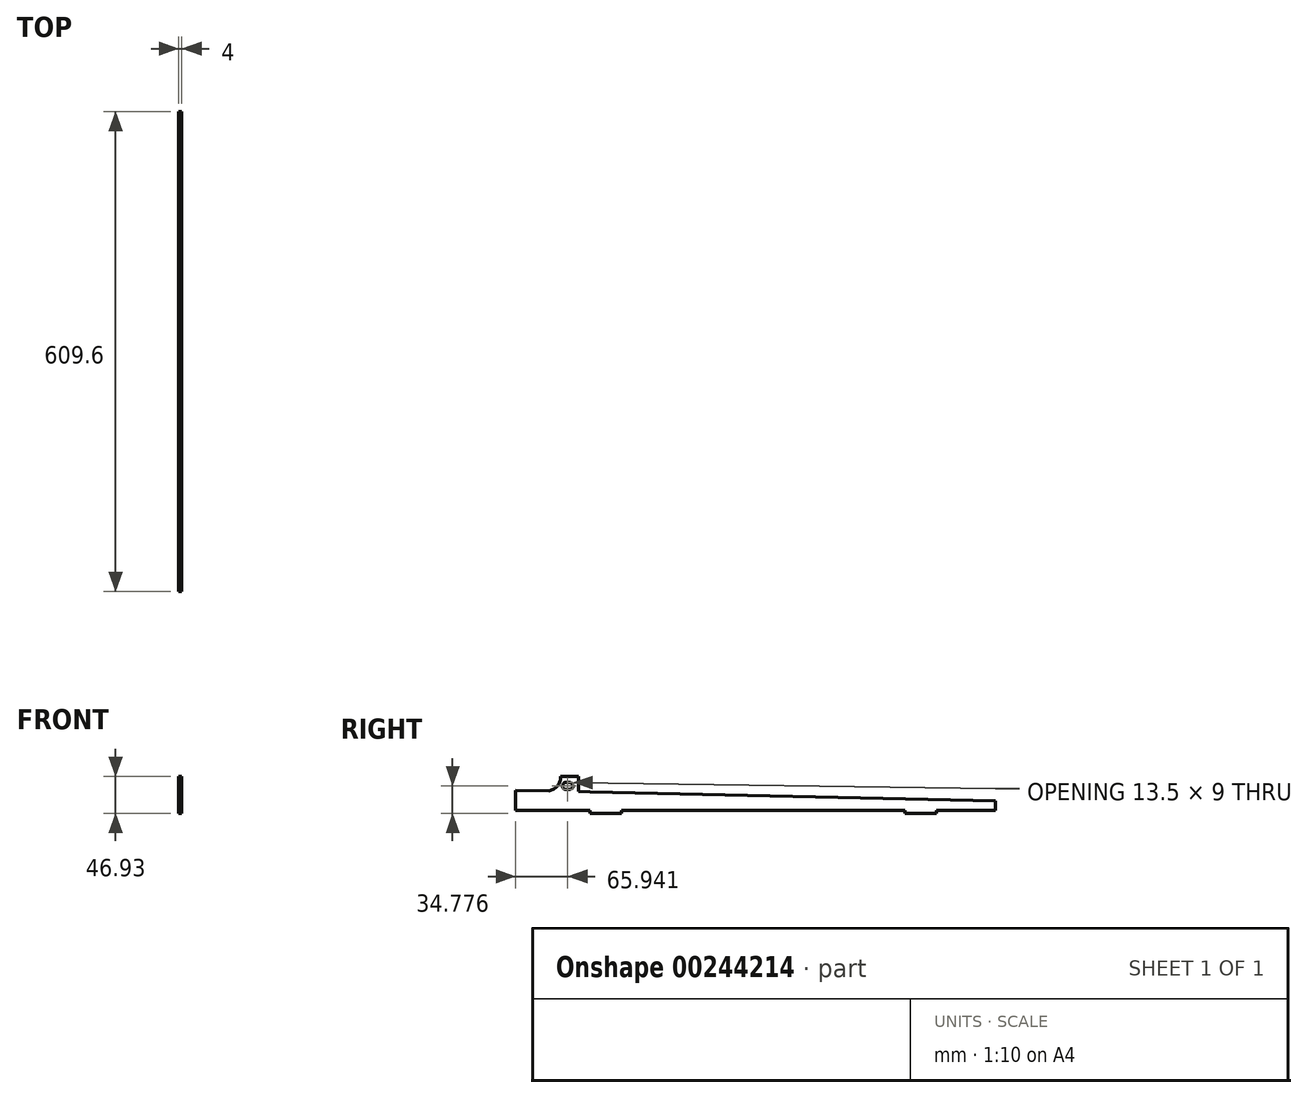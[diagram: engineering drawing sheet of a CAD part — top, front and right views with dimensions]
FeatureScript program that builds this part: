
annotation { "Feature Type Name" : "Feature", "Feature Type Description" : "" }
export const myFeature = defineFeature(function(context is Context, id is Id, definition is map)
    precondition{}
    {
        {
            var Q0;
            Q0=qCreatedBy(makeId("Right.planeOp"),FACE);
            var sketch = newSketch(context, id + "F0", { "sketchPlane" : qUnion([Q0])});
            skLineSegment(sketch, "E0", {"start": v(-3.89, 210.6) * mm, "end": v(7.32, -304.8) * mm});
            skLineSegment(sketch, "E1", {"start": v(7.32, -304.8) * mm, "end": v(19.46, -304.8) * mm});
            skLineSegment(sketch, "E2", {"start": v(19.46, -304.8) * mm, "end": v(19.46, -229.4) * mm});
            skLineSegment(sketch, "E3", {"start": v(19.46, -229.4) * mm, "end": v(23.46, -229.4) * mm});
            skLineSegment(sketch, "E4", {"start": v(23.46, -229.4) * mm, "end": v(23.46, -189.4) * mm});
            skLineSegment(sketch, "E5", {"start": v(23.46, -189.4) * mm, "end": v(19.46, -189.4) * mm});
            skLineSegment(sketch, "E6", {"start": v(19.46, -189.4) * mm, "end": v(19.46, 170.6) * mm});
            skLineSegment(sketch, "E7", {"start": v(19.46, 170.6) * mm, "end": v(23.46, 170.6) * mm});
            skLineSegment(sketch, "E8", {"start": v(23.46, 170.6) * mm, "end": v(23.46, 210.6) * mm});
            skLineSegment(sketch, "E9", {"start": v(23.46, 210.6) * mm, "end": v(19.46, 210.6) * mm});
            skLineSegment(sketch, "E10", {"start": v(19.46, 210.6) * mm, "end": v(19.46, 304.8) * mm});
            skLineSegment(sketch, "E11", {"start": v(19.46, 304.8) * mm, "end": v(-5.94, 304.8) * mm});
            skLineSegment(sketch, "E12", {"start": v(-5.94, 304.8) * mm, "end": v(-5.02, 262.4) * mm});
            skLineSegment(sketch, "E13", {"start": v(-5.02, 262.4) * mm, "end": v(-5.48, 260.67) * mm});
            skLineSegment(sketch, "E14", {"start": v(-5.48, 260.67) * mm, "end": v(-6.1, 259) * mm});
            skLineSegment(sketch, "E15", {"start": v(-6.1, 259) * mm, "end": v(-6.88, 257.38) * mm});
            skLineSegment(sketch, "E16", {"start": v(-6.88, 257.38) * mm, "end": v(-7.8, 255.85) * mm});
            skLineSegment(sketch, "E17", {"start": v(-7.8, 255.85) * mm, "end": v(-8.87, 254.4) * mm});
            skLineSegment(sketch, "E18", {"start": v(-8.87, 254.4) * mm, "end": v(-10.06, 253.07) * mm});
            skLineSegment(sketch, "E19", {"start": v(-10.06, 253.07) * mm, "end": v(-11.37, 251.85) * mm});
            skLineSegment(sketch, "E20", {"start": v(-11.37, 251.85) * mm, "end": v(-12.78, 250.75) * mm});
            skLineSegment(sketch, "E21", {"start": v(-12.78, 250.75) * mm, "end": v(-14.3, 249.8) * mm});
            skLineSegment(sketch, "E22", {"start": v(-14.3, 249.8) * mm, "end": v(-15.89, 248.97) * mm});
            skLineSegment(sketch, "E23", {"start": v(-15.89, 248.97) * mm, "end": v(-17.55, 248.3) * mm});
            skLineSegment(sketch, "E24", {"start": v(-17.55, 248.3) * mm, "end": v(-19.26, 247.8) * mm});
            skLineSegment(sketch, "E25", {"start": v(-19.26, 247.8) * mm, "end": v(-23.46, 247.8) * mm});
            skLineSegment(sketch, "E26", {"start": v(-23.46, 247.8) * mm, "end": v(-23.46, 224.8) * mm});
            skLineSegment(sketch, "E27", {"start": v(-23.46, 224.8) * mm, "end": v(-4.26, 224.8) * mm});
            skLineSegment(sketch, "E28", {"start": v(-4.26, 224.8) * mm, "end": v(-3.89, 210.6) * mm});
            skLineSegment(sketch, "E29", {"start": v(-15.21, 234.36) * mm, "end": v(-15.66, 235.45) * mm});
            skLineSegment(sketch, "E30", {"start": v(-15.66, 235.45) * mm, "end": v(-15.81, 241.11) * mm});
            skLineSegment(sketch, "E31", {"start": v(-15.81, 241.11) * mm, "end": v(-15.66, 242.28) * mm});
            skLineSegment(sketch, "E32", {"start": v(-15.66, 242.28) * mm, "end": v(-15.21, 243.36) * mm});
            skLineSegment(sketch, "E33", {"start": v(-15.21, 243.36) * mm, "end": v(-14.5, 244.3) * mm});
            skLineSegment(sketch, "E34", {"start": v(-14.5, 244.3) * mm, "end": v(-13.56, 245) * mm});
            skLineSegment(sketch, "E35", {"start": v(-13.56, 245) * mm, "end": v(-12.48, 245.46) * mm});
            skLineSegment(sketch, "E36", {"start": v(-12.48, 245.46) * mm, "end": v(-11.31, 245.61) * mm});
            skLineSegment(sketch, "E37", {"start": v(-11.31, 245.61) * mm, "end": v(-10.15, 245.46) * mm});
            skLineSegment(sketch, "E38", {"start": v(-10.15, 245.46) * mm, "end": v(-9.06, 245) * mm});
            skLineSegment(sketch, "E39", {"start": v(-9.06, 245) * mm, "end": v(-8.13, 244.3) * mm});
            skLineSegment(sketch, "E40", {"start": v(-8.13, 244.3) * mm, "end": v(-7.42, 243.36) * mm});
            skLineSegment(sketch, "E41", {"start": v(-7.42, 243.36) * mm, "end": v(-6.97, 242.28) * mm});
            skLineSegment(sketch, "E42", {"start": v(-6.97, 242.28) * mm, "end": v(-6.81, 241.11) * mm});
            skLineSegment(sketch, "E43", {"start": v(-6.81, 241.11) * mm, "end": v(-6.81, 236.61) * mm});
            skLineSegment(sketch, "E44", {"start": v(-6.81, 236.61) * mm, "end": v(-6.97, 235.45) * mm});
            skLineSegment(sketch, "E45", {"start": v(-6.97, 235.45) * mm, "end": v(-7.42, 234.36) * mm});
            skLineSegment(sketch, "E46", {"start": v(-7.42, 234.36) * mm, "end": v(-8.13, 233.43) * mm});
            skLineSegment(sketch, "E47", {"start": v(-8.13, 233.43) * mm, "end": v(-9.06, 232.71) * mm});
            skLineSegment(sketch, "E48", {"start": v(-9.06, 232.71) * mm, "end": v(-10.15, 232.26) * mm});
            skLineSegment(sketch, "E49", {"start": v(-10.15, 232.26) * mm, "end": v(-11.31, 232.11) * mm});
            skLineSegment(sketch, "E50", {"start": v(-11.31, 232.11) * mm, "end": v(-12.48, 232.26) * mm});
            skLineSegment(sketch, "E51", {"start": v(-12.48, 232.26) * mm, "end": v(-13.56, 232.71) * mm});
            skLineSegment(sketch, "E52", {"start": v(-13.56, 232.71) * mm, "end": v(-14.5, 233.43) * mm});
            skLineSegment(sketch, "E53", {"start": v(-14.5, 233.43) * mm, "end": v(-15.21, 234.36) * mm});
            skSolve(sketch);
        }
        {
            var Q0;
            Q0=makeQuery(id+"F0.imprint","IMPRINT",FACE,{"disambiguationData":[TD([[makeQuery(id+"F0.imprint","IMPRINT",EDGE,{"derivedFrom":sQuery(id+"F0.wireOp",EDGE,"E0")}),1.0]])]});
            extrude(context, id + "F1", {"entities" : qUnion([Q0]), "depth" : 4 * mm});
        }
        {
            var Q0;
            Q0=makeQuery(id+"F1.opExtrude","SWEPT_BODY",BODY,{"disambiguationData":[OSD([sQuery(id+"F0.wireOp",EDGE,"E0"),sQuery(id+"F0.wireOp",EDGE,"E1"),sQuery(id+"F0.wireOp",EDGE,"E2"),sQuery(id+"F0.wireOp",EDGE,"E3"),sQuery(id+"F0.wireOp",EDGE,"E4"),sQuery(id+"F0.wireOp",EDGE,"E5"),sQuery(id+"F0.wireOp",EDGE,"E6"),sQuery(id+"F0.wireOp",EDGE,"E7"),sQuery(id+"F0.wireOp",EDGE,"E8"),sQuery(id+"F0.wireOp",EDGE,"E9"),sQuery(id+"F0.wireOp",EDGE,"E10"),sQuery(id+"F0.wireOp",EDGE,"E11"),sQuery(id+"F0.wireOp",EDGE,"E12"),sQuery(id+"F0.wireOp",EDGE,"E13"),sQuery(id+"F0.wireOp",EDGE,"E14"),sQuery(id+"F0.wireOp",EDGE,"E15"),sQuery(id+"F0.wireOp",EDGE,"E16"),sQuery(id+"F0.wireOp",EDGE,"E17"),sQuery(id+"F0.wireOp",EDGE,"E18"),sQuery(id+"F0.wireOp",EDGE,"E19"),sQuery(id+"F0.wireOp",EDGE,"E20"),sQuery(id+"F0.wireOp",EDGE,"E21"),sQuery(id+"F0.wireOp",EDGE,"E22"),sQuery(id+"F0.wireOp",EDGE,"E23"),sQuery(id+"F0.wireOp",EDGE,"E24"),sQuery(id+"F0.wireOp",EDGE,"E25"),sQuery(id+"F0.wireOp",EDGE,"E26"),sQuery(id+"F0.wireOp",EDGE,"E27"),sQuery(id+"F0.wireOp",EDGE,"E28"),sQuery(id+"F0.wireOp",EDGE,"E29"),sQuery(id+"F0.wireOp",EDGE,"E30"),sQuery(id+"F0.wireOp",EDGE,"E31"),sQuery(id+"F0.wireOp",EDGE,"E32"),sQuery(id+"F0.wireOp",EDGE,"E33"),sQuery(id+"F0.wireOp",EDGE,"E34"),sQuery(id+"F0.wireOp",EDGE,"E35"),sQuery(id+"F0.wireOp",EDGE,"E36"),sQuery(id+"F0.wireOp",EDGE,"E37"),sQuery(id+"F0.wireOp",EDGE,"E38"),sQuery(id+"F0.wireOp",EDGE,"E39"),sQuery(id+"F0.wireOp",EDGE,"E40"),sQuery(id+"F0.wireOp",EDGE,"E41"),sQuery(id+"F0.wireOp",EDGE,"E42"),sQuery(id+"F0.wireOp",EDGE,"E43"),sQuery(id+"F0.wireOp",EDGE,"E44"),sQuery(id+"F0.wireOp",EDGE,"E45"),sQuery(id+"F0.wireOp",EDGE,"E46"),sQuery(id+"F0.wireOp",EDGE,"E47"),sQuery(id+"F0.wireOp",EDGE,"E48"),sQuery(id+"F0.wireOp",EDGE,"E49"),sQuery(id+"F0.wireOp",EDGE,"E50"),sQuery(id+"F0.wireOp",EDGE,"E51"),sQuery(id+"F0.wireOp",EDGE,"E52"),sQuery(id+"F0.wireOp",EDGE,"E53")])]});
            var Q1;
            Q1=makeQuery(id+"F1.opExtrude","SWEPT_EDGE",EDGE,{"disambiguationData":[OSD([sQuery(id+"F0.wireOp",EDGE,"E8"),sQuery(id+"F0.wireOp",EDGE,"E9")])]});
            transform(context, id + "F2", {"entities" : qUnion([Q0]), "transformType" : TransformType.ROTATION, "transformAxis" : qUnion([Q1]), "angle" : 90 * degree, "makeCopy" : false});
        }
        {
            var Q0;
            Q0=makeQuery(id+"F1.opExtrude","SWEPT_BODY",BODY,{"disambiguationData":[OSD([sQuery(id+"F0.wireOp",EDGE,"E0"),sQuery(id+"F0.wireOp",EDGE,"E1"),sQuery(id+"F0.wireOp",EDGE,"E2"),sQuery(id+"F0.wireOp",EDGE,"E3"),sQuery(id+"F0.wireOp",EDGE,"E4"),sQuery(id+"F0.wireOp",EDGE,"E5"),sQuery(id+"F0.wireOp",EDGE,"E6"),sQuery(id+"F0.wireOp",EDGE,"E7"),sQuery(id+"F0.wireOp",EDGE,"E8"),sQuery(id+"F0.wireOp",EDGE,"E9"),sQuery(id+"F0.wireOp",EDGE,"E10"),sQuery(id+"F0.wireOp",EDGE,"E11"),sQuery(id+"F0.wireOp",EDGE,"E12"),sQuery(id+"F0.wireOp",EDGE,"E13"),sQuery(id+"F0.wireOp",EDGE,"E14"),sQuery(id+"F0.wireOp",EDGE,"E15"),sQuery(id+"F0.wireOp",EDGE,"E16"),sQuery(id+"F0.wireOp",EDGE,"E17"),sQuery(id+"F0.wireOp",EDGE,"E18"),sQuery(id+"F0.wireOp",EDGE,"E19"),sQuery(id+"F0.wireOp",EDGE,"E20"),sQuery(id+"F0.wireOp",EDGE,"E21"),sQuery(id+"F0.wireOp",EDGE,"E22"),sQuery(id+"F0.wireOp",EDGE,"E23"),sQuery(id+"F0.wireOp",EDGE,"E24"),sQuery(id+"F0.wireOp",EDGE,"E25"),sQuery(id+"F0.wireOp",EDGE,"E26"),sQuery(id+"F0.wireOp",EDGE,"E27"),sQuery(id+"F0.wireOp",EDGE,"E28"),sQuery(id+"F0.wireOp",EDGE,"E29"),sQuery(id+"F0.wireOp",EDGE,"E30"),sQuery(id+"F0.wireOp",EDGE,"E31"),sQuery(id+"F0.wireOp",EDGE,"E32"),sQuery(id+"F0.wireOp",EDGE,"E33"),sQuery(id+"F0.wireOp",EDGE,"E34"),sQuery(id+"F0.wireOp",EDGE,"E35"),sQuery(id+"F0.wireOp",EDGE,"E36"),sQuery(id+"F0.wireOp",EDGE,"E37"),sQuery(id+"F0.wireOp",EDGE,"E38"),sQuery(id+"F0.wireOp",EDGE,"E39"),sQuery(id+"F0.wireOp",EDGE,"E40"),sQuery(id+"F0.wireOp",EDGE,"E41"),sQuery(id+"F0.wireOp",EDGE,"E42"),sQuery(id+"F0.wireOp",EDGE,"E43"),sQuery(id+"F0.wireOp",EDGE,"E44"),sQuery(id+"F0.wireOp",EDGE,"E45"),sQuery(id+"F0.wireOp",EDGE,"E46"),sQuery(id+"F0.wireOp",EDGE,"E47"),sQuery(id+"F0.wireOp",EDGE,"E48"),sQuery(id+"F0.wireOp",EDGE,"E49"),sQuery(id+"F0.wireOp",EDGE,"E50"),sQuery(id+"F0.wireOp",EDGE,"E51"),sQuery(id+"F0.wireOp",EDGE,"E52"),sQuery(id+"F0.wireOp",EDGE,"E53")])]});
            var Q1;
            Q1=makeQuery(id+"F1.opExtrude","CAP_EDGE",EDGE,{"disambiguationData":[OSD([sQuery(id+"F0.wireOp",EDGE,"E11")])],"isStart":true});
            transform(context, id + "F3", {"entities" : qUnion([Q0]), "transformType" : TransformType.ROTATION, "transformAxis" : qUnion([Q1]), "angle" : 180 * degree, "makeCopy" : false});
        }
    });
